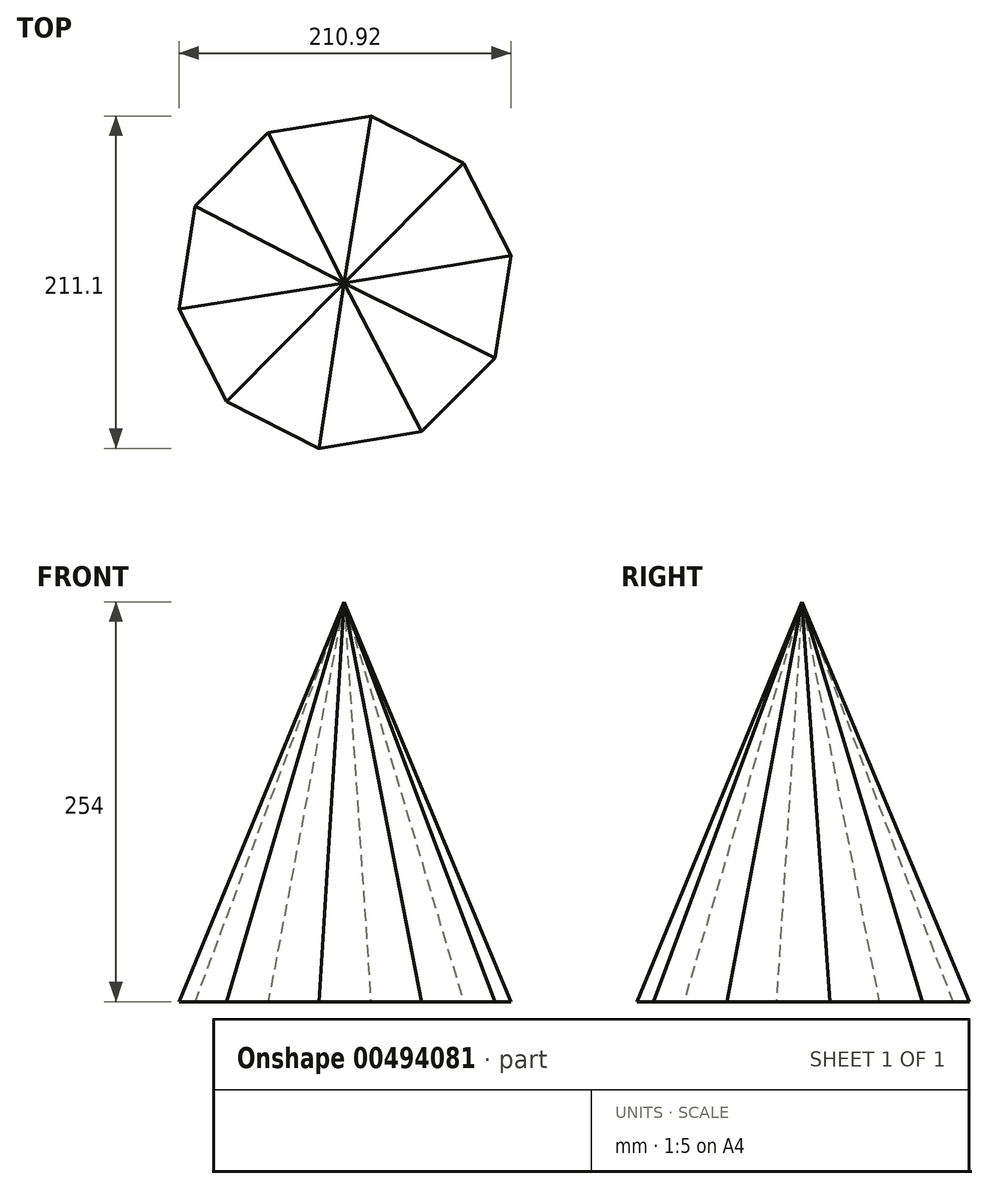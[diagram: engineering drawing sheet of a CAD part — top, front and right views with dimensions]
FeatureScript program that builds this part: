
annotation { "Feature Type Name" : "Feature", "Feature Type Description" : "" }
export const myFeature = defineFeature(function(context is Context, id is Id, definition is map)
    precondition{}
    {
        {
            var Q0;
            Q0=qCreatedBy(makeId("Top.planeOp"),FACE);
            var sketch = newSketch(context, id + "F0", { "sketchPlane" : qUnion([Q0])});
            skCircle(sketch, "E0.cCircle", {"center": v(0, 0) * mm, "radius": 106.82 * mm, "construction": true});
            skLineSegment(sketch, "E0.0", {"start": v(-95.31, 48.24) * mm, "end": v(-48.76, 95.05) * mm});
            skLineSegment(sketch, "E0.1", {"start": v(-48.76, 95.05) * mm, "end": v(16.43, 105.55) * mm});
            skLineSegment(sketch, "E0.2", {"start": v(16.43, 105.55) * mm, "end": v(75.33, 75.74) * mm});
            skLineSegment(sketch, "E0.3", {"start": v(75.33, 75.74) * mm, "end": v(105.46, 17) * mm});
            skLineSegment(sketch, "E0.4", {"start": v(105.46, 17) * mm, "end": v(95.31, -48.24) * mm});
            skLineSegment(sketch, "E0.5", {"start": v(95.31, -48.24) * mm, "end": v(48.76, -95.05) * mm});
            skLineSegment(sketch, "E0.6", {"start": v(48.76, -95.05) * mm, "end": v(-16.43, -105.55) * mm});
            skLineSegment(sketch, "E0.7", {"start": v(-16.43, -105.55) * mm, "end": v(-75.33, -75.74) * mm});
            skLineSegment(sketch, "E0.8", {"start": v(-75.33, -75.74) * mm, "end": v(-105.46, -17) * mm});
            skLineSegment(sketch, "E0.9", {"start": v(-105.46, -17) * mm, "end": v(-95.31, 48.24) * mm});
            skSolve(sketch);
        }
        {
            var Q0;
            Q0=qCreatedBy(makeId("Top.planeOp"),FACE);
            cPlane(context, id + "F1", {"entities" : qUnion([Q0]), "cplaneType" : CPlaneType.OFFSET, "offset" : 254 * mm, "width" : 152.4 * mm, "height" : 152.4 * mm});
        }
        {
            var Q0;
            Q0=qCreatedBy(id+"F1.planeOp",FACE);
            var sketch = newSketch(context, id + "F2", { "sketchPlane" : qUnion([Q0])});
            skPoint(sketch, "E1", {"position": v(-0.58, -0.73) * mm});
            skSolve(sketch);
        }
        {
            var Q0;
            Q0=sQuery(id+"F2.wireOp",VERTEX,"E1");
            var Q1;
            Q1=makeQuery(id+"F0.imprint","IMPRINT",FACE,{"disambiguationData":[TD([[makeQuery(id+"F0.imprint","IMPRINT",EDGE,{"derivedFrom":sQuery(id+"F0.wireOp",EDGE,"E0.0")}),-1.0]])]});
            loft(context, id + "F3", {"sheetProfilesArray" : [{ "sheetProfileEntities" : qUnion([Q0]) }, { "sheetProfileEntities" : qUnion([Q1]) }]});
        }
    });
